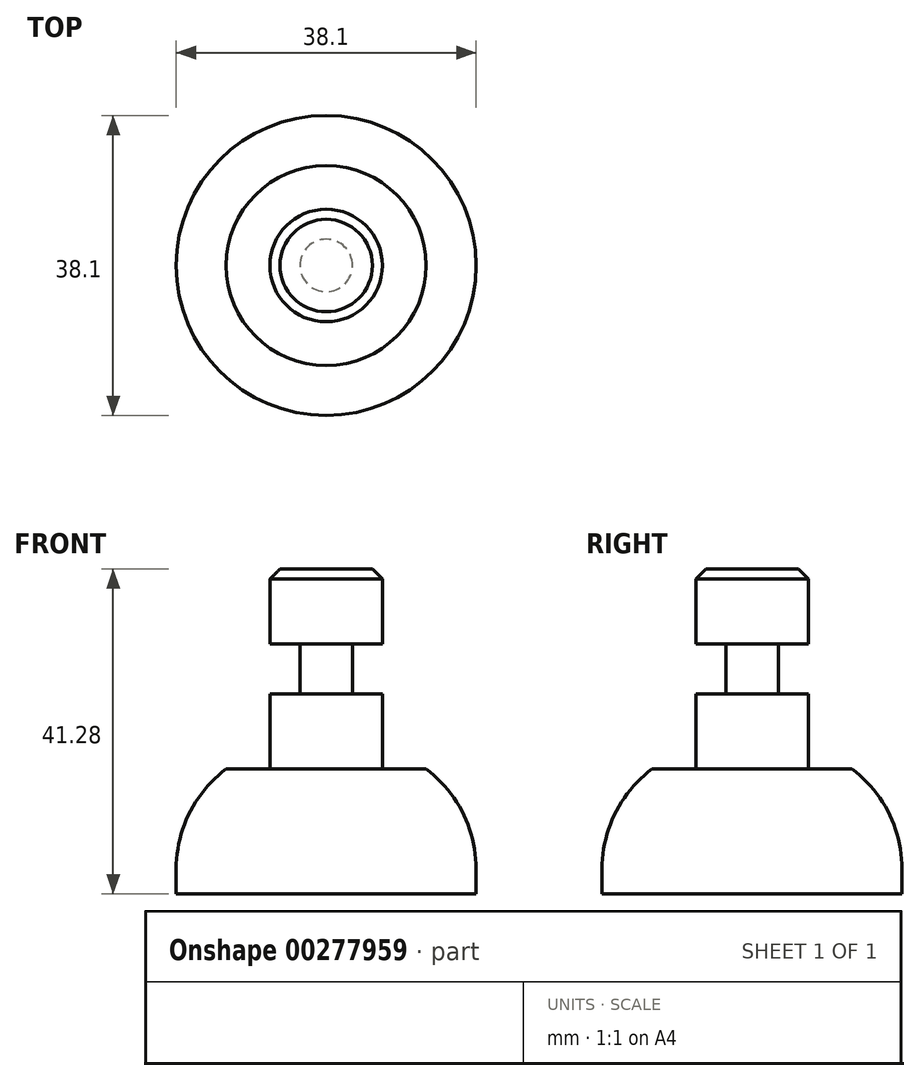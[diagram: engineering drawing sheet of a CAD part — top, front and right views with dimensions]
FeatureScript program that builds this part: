
annotation { "Feature Type Name" : "Feature", "Feature Type Description" : "" }
export const myFeature = defineFeature(function(context is Context, id is Id, definition is map)
    precondition{}
    {
        {
            var Q0;
            Q0=qCreatedBy(makeId("Front.planeOp"),FACE);
            var sketch = newSketch(context, id + "F0", { "sketchPlane" : qUnion([Q0])});
            skLineSegment(sketch, "E0", {"start": v(0, 56.05) * mm, "end": v(0, -58.93) * mm, "construction": true});
            skLineSegment(sketch, "E1", {"start": v(-116, 0) * mm, "end": v(94.9, 0) * mm, "construction": true});
            skLineSegment(sketch, "E2", {"start": v(0, 0) * mm, "end": v(19.05, 0) * mm});
            skLineSegment(sketch, "E3", {"start": v(19.05, 0) * mm, "end": v(19.05, 3.17) * mm});
            skArc(sketch, "E4", {"start": v(19.05, 3.18) * mm, "mid": v(17.37, 10.27) * mm, "end": v(12.7, 15.88) * mm});
            skLineSegment(sketch, "E5", {"start": v(12.7, 15.87) * mm, "end": v(7.14, 15.87) * mm});
            skLineSegment(sketch, "E6", {"start": v(7.14, 15.87) * mm, "end": v(7.14, 25.4) * mm});
            skLineSegment(sketch, "E7", {"start": v(7.14, 25.4) * mm, "end": v(3.34, 25.4) * mm});
            skLineSegment(sketch, "E8", {"start": v(3.34, 25.4) * mm, "end": v(3.34, 31.75) * mm});
            skLineSegment(sketch, "E9", {"start": v(3.34, 31.75) * mm, "end": v(7.14, 31.75) * mm});
            skLineSegment(sketch, "E10", {"start": v(7.14, 31.75) * mm, "end": v(7.14, 41.27) * mm});
            skLineSegment(sketch, "E11", {"start": v(7.14, 41.28) * mm, "end": v(0, 41.28) * mm});
            skLineSegment(sketch, "E12", {"start": v(0, 41.28) * mm, "end": v(0, 0) * mm});
            skSolve(sketch);
        }
        {
            var Q0;
            Q0=makeQuery(id+"F0.imprint","IMPRINT",FACE,{"disambiguationData":[TD([[makeQuery(id+"F0.imprint","IMPRINT",EDGE,{"derivedFrom":sQuery(id+"F0.wireOp",EDGE,"E2")}),1.0]])]});
            var Q1;
            Q1=sQuery(id+"F0.wireOp",EDGE,"E0");
            revolve(context, id + "F1", {"entities" : qUnion([Q0]), "axis" : qUnion([Q1]), "revolveType" : RevolveType.FULL});
        }
        {
            var Q0;
            Q0=makeQuery(id+"F1.opRevolve","SWEPT_EDGE",EDGE,{"disambiguationData":[OSD([sQuery(id+"F0.wireOp",EDGE,"E5"),sQuery(id+"F0.wireOp",EDGE,"E6")])]});
            fillet(context, id + "F2", {"entities" : qUnion([Q0]), "radius" : 0.25 * mm, "tangentPropagation" : true, "allowEdgeOverflow" : false});
        }
        {
            var Q0;
            Q0=makeQuery(id+"F1.opRevolve","SWEPT_EDGE",EDGE,{"disambiguationData":[OSD([sQuery(id+"F0.wireOp",EDGE,"E10"),sQuery(id+"F0.wireOp",EDGE,"E11")])]});
            chamfer(context, id + "F3", {"entities" : qUnion([Q0]), "chamferType" : ChamferType.OFFSET_ANGLE, "width" : 1.27 * mm, "oppositeDirection" : false, "angle" : 45 * degree, "tangentPropagation" : true});
        }
    });
